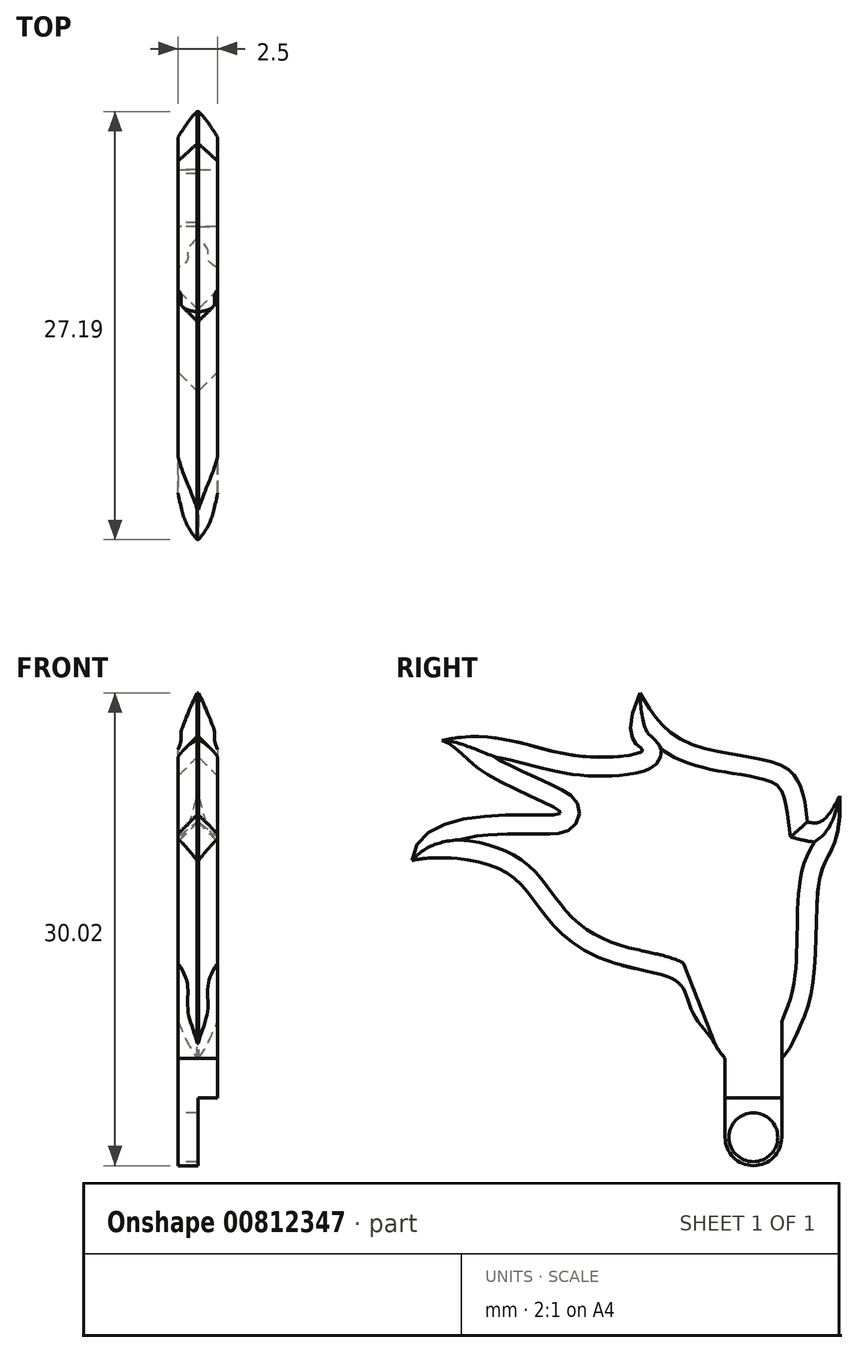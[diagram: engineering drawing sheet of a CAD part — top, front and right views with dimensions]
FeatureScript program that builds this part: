
annotation { "Feature Type Name" : "Feature", "Feature Type Description" : "" }
export const myFeature = defineFeature(function(context is Context, id is Id, definition is map)
    precondition{}
    {
        {
            var Q0;
            Q0=qCreatedBy(makeId("Right.planeOp"),FACE);
            var sketch = newSketch(context, id + "F0", { "sketchPlane" : qUnion([Q0])});
            skFitSpline(sketch, "E0", {"points": [v(-10.47, -10.38) * mm, v(-9.58, -8.94) * mm, v(-8.45, -5.33) * mm, v(-7.98, 1.43) * mm, v(-6.78, 6.3) * mm], "startDerivative": vector(6.72, 6.45) * mm, "endDerivative": vector(-1.54, 34.49) * mm});
            skFitSpline(sketch, "E1", {"points": [v(-6.78, 6.3) * mm, v(-7.93, 4.72) * mm, v(-8.84, 4.66) * mm], "startDerivative": vector(-1.54, -3.12) * mm, "endDerivative": vector(-2.4, 0.61) * mm});
            skFitSpline(sketch, "E2", {"points": [v(-8.84, 4.66) * mm, v(-9.24, 6.8) * mm, v(-10.45, 8.21) * mm, v(-16.7, 9.8) * mm, v(-19.5, 12.84) * mm], "startDerivative": vector(-2.68, 19.98) * mm, "endDerivative": vector(-6.35, 10.43) * mm});
            skFitSpline(sketch, "E3", {"points": [v(-19.5, 12.84) * mm, v(-19.3, 9.18) * mm, v(-23.5, 8.85) * mm, v(-32.06, 9.82) * mm], "startDerivative": vector(-16.05, -34.53) * mm, "endDerivative": vector(-24.4, -6) * mm});
            skFitSpline(sketch, "E4", {"points": [v(-32.06, 9.82) * mm, v(-29.19, 7.68) * mm, v(-24.6, 5.17) * mm, v(-33.96, 2.2) * mm], "startDerivative": vector(11.03, -2.83) * mm, "endDerivative": vector(-2.35, -27.04) * mm});
            skFitSpline(sketch, "E5", {"points": [v(-33.96, 2.2) * mm, v(-31.24, 2.34) * mm, v(-27.8, 1.33) * mm, v(-25.7, -1.02) * mm, v(-19.75, -4.67) * mm], "startDerivative": vector(7.87, 2.18) * mm, "endDerivative": vector(31.6, -6.43) * mm});
            skFitSpline(sketch, "E6", {"points": [v(-19.75, -4.67) * mm, v(-16.74, -5.91) * mm, v(-16, -7.7) * mm, v(-14.74, -9.4) * mm], "startDerivative": vector(15.77, -3.24) * mm, "endDerivative": vector(2.9, -5.06) * mm});
            skLineSegment(sketch, "E7.left", {"start": v(-14.07, -10.38) * mm, "end": v(-14.07, -15.38) * mm});
            skLineSegment(sketch, "E7.right", {"start": v(-10.47, -10.38) * mm, "end": v(-10.47, -15.38) * mm});
            skArc(sketch, "E8", {"start": v(-10.47, -15.38) * mm, "mid": v(-12.27, -17.18) * mm, "end": v(-14.07, -15.38) * mm});
            skFitSpline(sketch, "E9", {"points": [v(-14.74, -9.4) * mm, v(-14.65, -9.6) * mm, v(-14.07, -10.38) * mm], "startDerivative": vector(0.2, -0.51) * mm, "endDerivative": vector(1.03, -1.33) * mm});
            skSolve(sketch);
        }
        {
            var Q0;
            Q0=makeQuery(id+"F0.imprint","IMPRINT",FACE,{"disambiguationData":[TD([[makeQuery(id+"F0.imprint","IMPRINT",EDGE,{"derivedFrom":sQuery(id+"F0.wireOp",EDGE,"E0")}),1.0]])]});
            extrude(context, id + "F1", {"entities" : qUnion([Q0]), "depth" : 2.5 * mm, "offsetDistance" : 25 * mm, "symmetric" : true});
        }
        {
            var Q0;
            Q0=makeQuery(id+"F1.opExtrude","CAP_EDGE",EDGE,{"disambiguationData":[OSD([sQuery(id+"F0.wireOp",EDGE,"E1")])],"isStart":true});
            var Q1;
            Q1=makeQuery(id+"F1.opExtrude","CAP_EDGE",EDGE,{"disambiguationData":[OSD([sQuery(id+"F0.wireOp",EDGE,"E1")])],"isStart":false});
            var Q2;
            Q2=makeQuery(id+"F1.opExtrude","CAP_EDGE",EDGE,{"disambiguationData":[OSD([sQuery(id+"F0.wireOp",EDGE,"E0")])],"isStart":true});
            var Q3;
            Q3=makeQuery(id+"F1.opExtrude","CAP_EDGE",EDGE,{"disambiguationData":[OSD([sQuery(id+"F0.wireOp",EDGE,"E0")])],"isStart":false});
            var Q4;
            Q4=makeQuery(id+"F1.opExtrude","CAP_EDGE",EDGE,{"disambiguationData":[OSD([sQuery(id+"F0.wireOp",EDGE,"E2")])],"isStart":true});
            var Q5;
            Q5=makeQuery(id+"F1.opExtrude","CAP_EDGE",EDGE,{"disambiguationData":[OSD([sQuery(id+"F0.wireOp",EDGE,"E2")])],"isStart":false});
            var Q6;
            Q6=makeQuery(id+"F1.opExtrude","CAP_EDGE",EDGE,{"disambiguationData":[OSD([sQuery(id+"F0.wireOp",EDGE,"E3")])],"isStart":false});
            var Q7;
            Q7=makeQuery(id+"F1.opExtrude","CAP_EDGE",EDGE,{"disambiguationData":[OSD([sQuery(id+"F0.wireOp",EDGE,"E3")])],"isStart":true});
            var Q8;
            Q8=makeQuery(id+"F1.opExtrude","CAP_EDGE",EDGE,{"disambiguationData":[OSD([sQuery(id+"F0.wireOp",EDGE,"E4")])],"isStart":false});
            var Q9;
            Q9=makeQuery(id+"F1.opExtrude","CAP_EDGE",EDGE,{"disambiguationData":[OSD([sQuery(id+"F0.wireOp",EDGE,"E4")])],"isStart":true});
            chamfer(context, id + "F2", {"entities" : qUnion([Q0, Q1, Q2, Q3, Q4, Q5, Q6, Q7, Q8, Q9]), "width" : 1.2 * mm, "tangentPropagation" : true});
        }
        {
            var Q0;
            Q0=makeQuery(id+"F1.opExtrude","CAP_FACE",FACE,{"disambiguationData":[OSD([sQuery(id+"F0.wireOp",EDGE,"E0"),sQuery(id+"F0.wireOp",EDGE,"E1"),sQuery(id+"F0.wireOp",EDGE,"E2"),sQuery(id+"F0.wireOp",EDGE,"E3"),sQuery(id+"F0.wireOp",EDGE,"E4"),sQuery(id+"F0.wireOp",EDGE,"E5"),sQuery(id+"F0.wireOp",EDGE,"E6"),sQuery(id+"F0.wireOp",EDGE,"E7.left"),sQuery(id+"F0.wireOp",EDGE,"E7.right"),sQuery(id+"F0.wireOp",EDGE,"b68a347e-6c9d-4fff-a1d8-a2c3c59c421b"),sQuery(id+"F0.wireOp",EDGE,"E8")])],"isStart":true});
            var sketch = newSketch(context, id + "F3", { "sketchPlane" : qUnion([Q0])});
            skPoint(sketch, "E10", {"position": v(12.27, -15.38) * mm});
            skCircle(sketch, "E11", {"center": v(12.27, -15.38) * mm, "radius": 1.55 * mm});
            skSolve(sketch);
        }
        {
            var Q0;
            Q0 = qSketchRegion(id + "F3", true);
            extrude(context, id + "F4", {"entities" : qUnion([Q0]), "operationType" : NewBodyOperationType.REMOVE, "oppositeDirection" : true, "depth" : 5 * mm, "offsetDistance" : 25 * mm});
        }
        {
            var Q0;
            Q0=makeQuery(id+"F1.opExtrude","CAP_FACE",FACE,{"disambiguationData":[OSD([sQuery(id+"F0.wireOp",EDGE,"E0"),sQuery(id+"F0.wireOp",EDGE,"E1"),sQuery(id+"F0.wireOp",EDGE,"E2"),sQuery(id+"F0.wireOp",EDGE,"E3"),sQuery(id+"F0.wireOp",EDGE,"E4"),sQuery(id+"F0.wireOp",EDGE,"E5"),sQuery(id+"F0.wireOp",EDGE,"E6"),sQuery(id+"F0.wireOp",EDGE,"E7.left"),sQuery(id+"F0.wireOp",EDGE,"E7.right"),sQuery(id+"F0.wireOp",EDGE,"b68a347e-6c9d-4fff-a1d8-a2c3c59c421b"),sQuery(id+"F0.wireOp",EDGE,"E8")])],"isStart":false});
            var sketch = newSketch(context, id + "F5", { "sketchPlane" : qUnion([Q0])});
            skLineSegment(sketch, "E12", {"start": v(-14.07, -15.38) * mm, "end": v(-14.07, -12.88) * mm});
            skLineSegment(sketch, "E13", {"start": v(-14.07, -12.88) * mm, "end": v(-10.47, -12.88) * mm});
            skLineSegment(sketch, "E14", {"start": v(-10.47, -12.88) * mm, "end": v(-10.47, -15.38) * mm});
            skArc(sketch, "E15", {"start": v(-14.07, -15.38) * mm, "mid": v(-12.27, -17.18) * mm, "end": v(-10.47, -15.38) * mm});
            skSolve(sketch);
        }
        {
            var Q0;
            Q0 = qSketchRegion(id + "F5", true);
            extrude(context, id + "F6", {"entities" : qUnion([Q0]), "operationType" : NewBodyOperationType.REMOVE, "oppositeDirection" : true, "depth" : (2.5 / 2) * mm, "offsetDistance" : 25 * mm});
        }
        {
            var Q0;
            Q0=makeQuery(id+"F1.opExtrude","CAP_EDGE",EDGE,{"disambiguationData":[OSD([sQuery(id+"F0.wireOp",EDGE,"E6")])],"isStart":true});
            var Q1;
            Q1=makeQuery(id+"F1.opExtrude","CAP_EDGE",EDGE,{"disambiguationData":[OSD([sQuery(id+"F0.wireOp",EDGE,"E5")])],"isStart":true});
            var Q2;
            Q2=makeQuery(id+"F1.opExtrude","CAP_EDGE",EDGE,{"disambiguationData":[OSD([sQuery(id+"F0.wireOp",EDGE,"E5")])],"isStart":false});
            var Q3;
            Q3=makeQuery(id+"F1.opExtrude","CAP_EDGE",EDGE,{"disambiguationData":[OSD([sQuery(id+"F0.wireOp",EDGE,"E6")])],"isStart":false});
            chamfer(context, id + "F7", {"entities" : qUnion([Q0, Q1, Q2, Q3]), "width" : 1.2 * mm, "tangentPropagation" : true});
        }
    });
